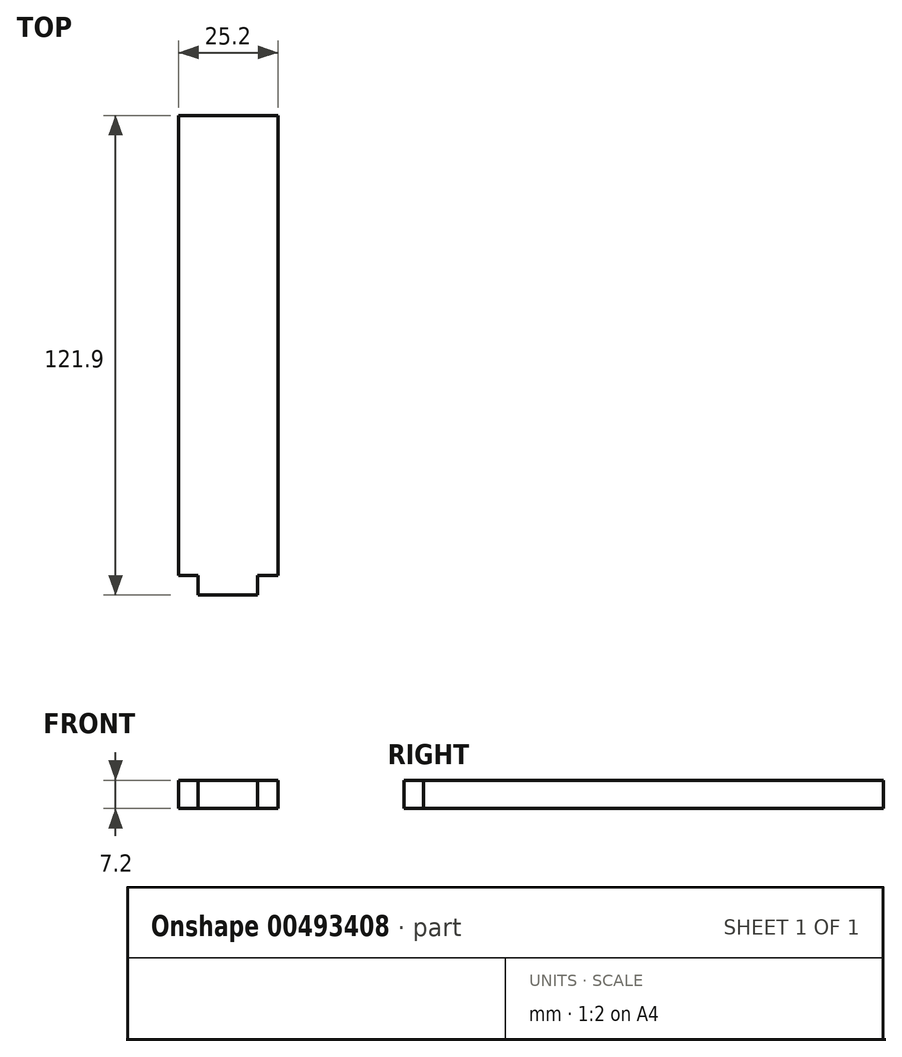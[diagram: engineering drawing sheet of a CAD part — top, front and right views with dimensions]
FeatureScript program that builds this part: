
annotation { "Feature Type Name" : "Feature", "Feature Type Description" : "" }
export const myFeature = defineFeature(function(context is Context, id is Id, definition is map)
    precondition{}
    {
        {
            var Q0;
            Q0=qCreatedBy(makeId("Front.planeOp"),FACE);
            var sketch = newSketch(context, id + "F0", { "sketchPlane" : qUnion([Q0])});
            skLineSegment(sketch, "E0.bottom", {"start": v(-40.67, 7.2) * mm, "end": v(-15.47, 7.2) * mm});
            skLineSegment(sketch, "E0.top", {"start": v(-40.67, 0) * mm, "end": v(-15.47, 0) * mm});
            skLineSegment(sketch, "E0.left", {"start": v(-40.67, 7.2) * mm, "end": v(-40.67, 0) * mm});
            skLineSegment(sketch, "E0.right", {"start": v(-15.47, 7.2) * mm, "end": v(-15.47, 0) * mm});
            skSolve(sketch);
        }
        {
            var Q0;
            Q0 = qSketchRegion(id + "F0", true);
            extrude(context, id + "F1", {"entities" : qUnion([Q0]), "endBound" : BoundingType.SYMMETRIC, "depth" : 116.9 * mm});
        }
        {
            var Q0;
            Q0=makeQuery(id+"F1.opExtrude","CAP_FACE",FACE,{"disambiguationData":[OSD([sQuery(id+"F0.wireOp",EDGE,"E0.bottom"),sQuery(id+"F0.wireOp",EDGE,"E0.top"),sQuery(id+"F0.wireOp",EDGE,"E0.left"),sQuery(id+"F0.wireOp",EDGE,"E0.right")])],"isStart":false});
            var sketch = newSketch(context, id + "F2", { "sketchPlane" : qUnion([Q0])});
            skLineSegment(sketch, "E1.bottom", {"start": v(-35.69, 7.2) * mm, "end": v(-20.6, 7.2) * mm});
            skLineSegment(sketch, "E1.top", {"start": v(-35.69, 0) * mm, "end": v(-20.6, 0) * mm});
            skLineSegment(sketch, "E1.left", {"start": v(-35.69, 7.2) * mm, "end": v(-35.69, 0) * mm});
            skLineSegment(sketch, "E1.right", {"start": v(-20.6, 7.2) * mm, "end": v(-20.6, 0) * mm});
            skSolve(sketch);
        }
        {
            var Q0;
            Q0 = qSketchRegion(id + "F2", true);
            extrude(context, id + "F3", {"entities" : qUnion([Q0]), "operationType" : NewBodyOperationType.ADD, "depth" : 5 * mm});
        }
    });
